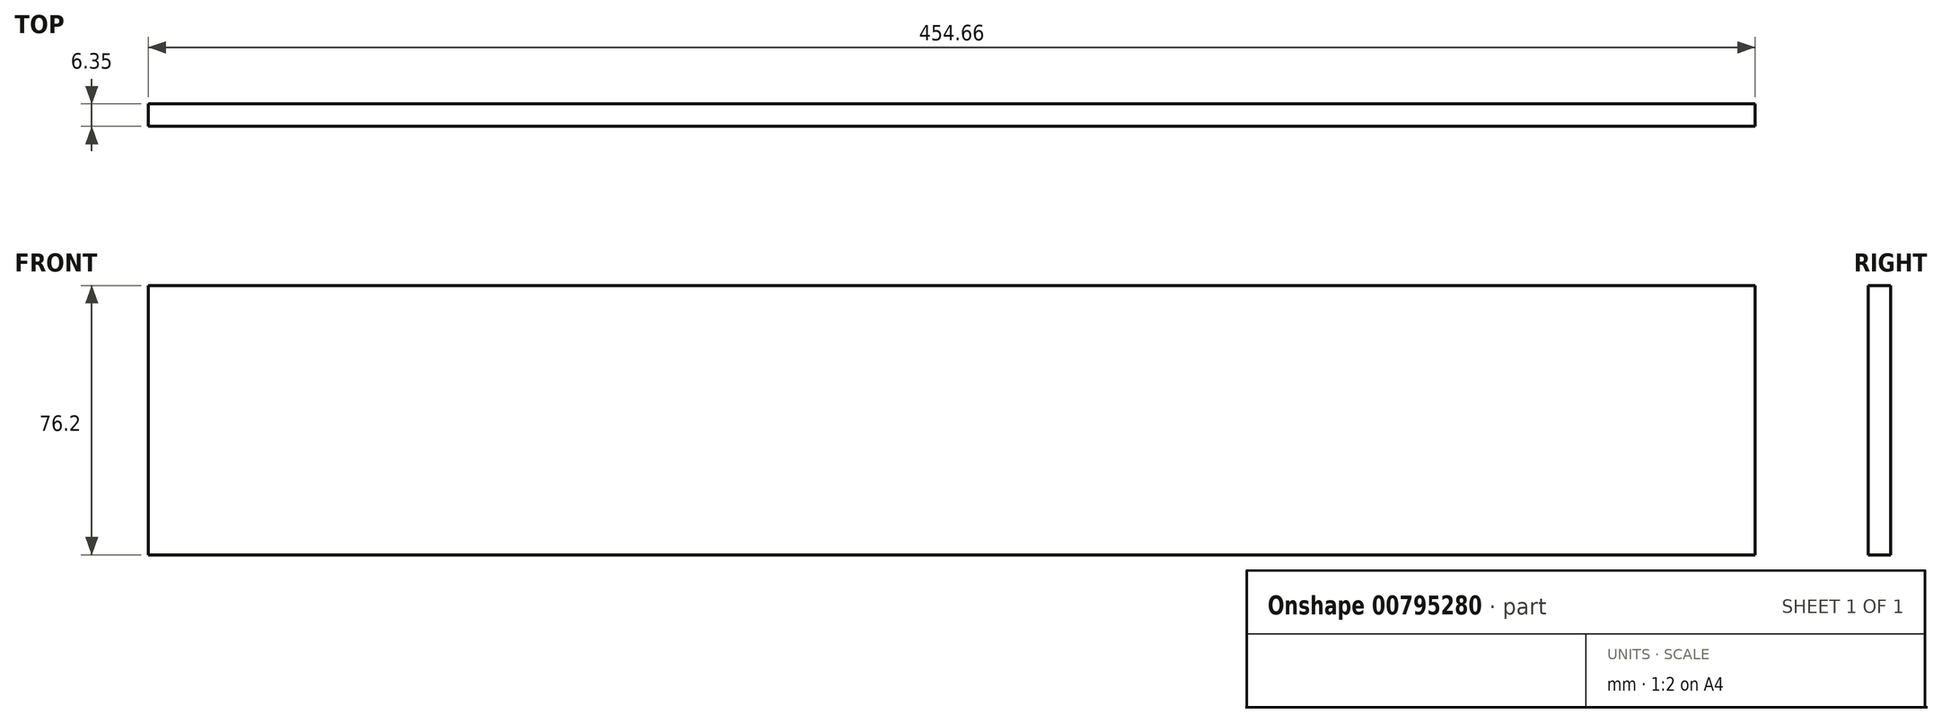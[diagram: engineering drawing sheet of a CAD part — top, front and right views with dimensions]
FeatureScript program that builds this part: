
annotation { "Feature Type Name" : "Feature", "Feature Type Description" : "" }
export const myFeature = defineFeature(function(context is Context, id is Id, definition is map)
    precondition{}
    {
        {
            var Q0;
            Q0=qCreatedBy(makeId("Front.planeOp"),FACE);
            var sketch = newSketch(context, id + "F0", { "sketchPlane" : qUnion([Q0])});
            skLineSegment(sketch, "E0.bottom", {"start": v(227.33, -38.1) * mm, "end": v(-227.33, -38.1) * mm});
            skLineSegment(sketch, "E0.top", {"start": v(227.33, 38.1) * mm, "end": v(-227.33, 38.1) * mm});
            skLineSegment(sketch, "E0.left", {"start": v(227.33, -38.1) * mm, "end": v(227.33, 38.1) * mm});
            skLineSegment(sketch, "E0.right", {"start": v(-227.33, -38.1) * mm, "end": v(-227.33, 38.1) * mm});
            skPoint(sketch, "E0.middle", {"position": v(0, 0) * mm});
            skSolve(sketch);
        }
        {
            var Q0;
            Q0 = qSketchRegion(id + "F0", true);
            extrude(context, id + "F1", {"entities" : qUnion([Q0]), "depth" : 6.35 * mm, "offsetDistance" : 25.4 * mm});
        }
    });
